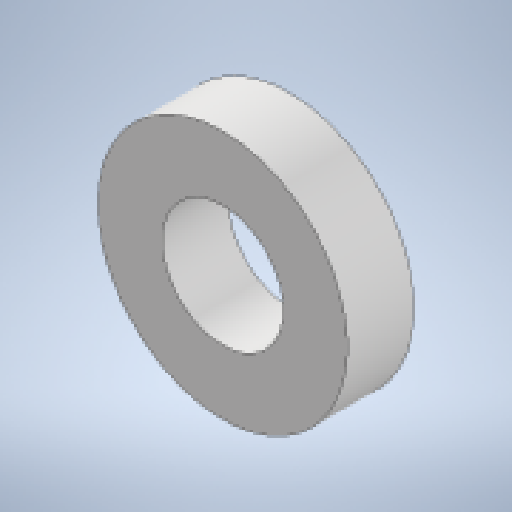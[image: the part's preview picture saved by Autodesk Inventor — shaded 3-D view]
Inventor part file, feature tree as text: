
AUTODESK INVENTOR PART (.ipt)
format: ipt  version: 2023 (Build 270158000, 158)  size: 137,216 bytes
history: native  units: in
note: dims shown in document units (in); Inventor stores cm internally (conversion verified against a paired STEP export)
features: extrude x1, sketch x1
ambient origin geometry x8: Origin, YZ Plane, XZ Plane, XY Plane, X Axis, Y Axis, Z Axis, Center Point
bodies: Solid1 (feature_tree)
feature tree (2):
  extrude  "Extrusion1"  Depth=0.1in
  sketch  "Sketch1"  dims[d0=0.126in d1=0.126in d2=0.182in d3=0.375in d4=0.1in d5=0.0in]
